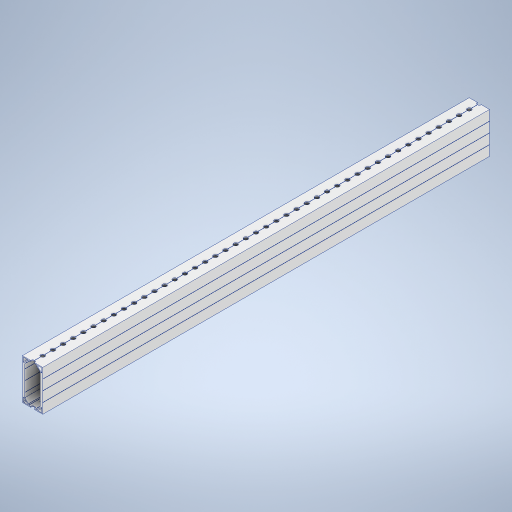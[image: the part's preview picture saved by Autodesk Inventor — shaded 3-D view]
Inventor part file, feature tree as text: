
AUTODESK INVENTOR PART (.ipt)
format: ipt  version: 2024 (Build 280153000, 153)  size: 935,936 bytes
history: native  units: in
note: dims shown in document units (in); Inventor stores cm internally (conversion verified against a paired STEP export)
features: extrude x2, sketch x2, other x1
ambient origin geometry x8: Origin, YZ Plane, XZ Plane, XY Plane, X Axis, Y Axis, Z Axis, Center Point
bodies: Solid1 (feature_tree)
feature tree (5):
  extrude  "Extrusion1"  Depth=1.0in TaperAngle=0.0deg
  extrude  "Extrusion2"  [1 undecoded]
  sketch  "Sketch1"  dims[d0=24.0in d1=0.0in d2=1.0in d3=0.0in]
  sketch  "Sketch2"
  other  "Internal Fillets"
note: 1 required parameter value undecoded (feature->parameter linkage not recoverable at this tier; creation-order binding heuristic only, values carry confidence <= 0.55)
